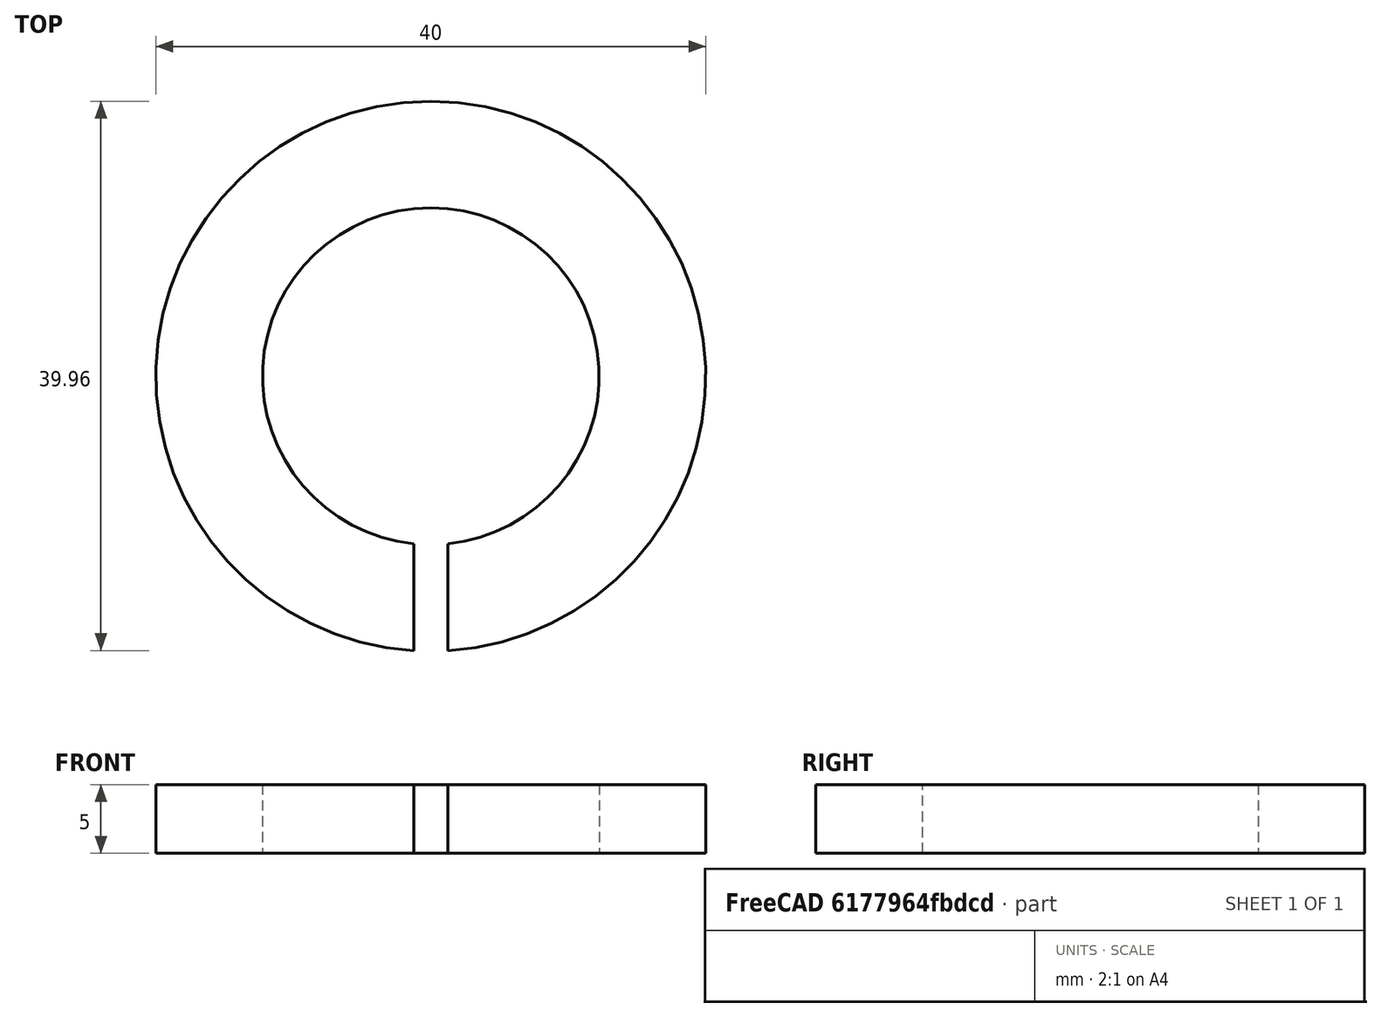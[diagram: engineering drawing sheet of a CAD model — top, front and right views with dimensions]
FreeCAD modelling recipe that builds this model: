
FCSTD DOCUMENT  (FreeCAD 0.15R4651 (Git))
Label: Federring_DIN127-B24
License: All rights reserved
LicenseURL: http://de.wikipedia.org/wiki/Alle_Rechte_vorbehalten
objects: Sketcher::SketchObject×1, PartDesign::Pad×1
note: 3 computed .brp shape members not serialized (recipe doc carries the construction recipe); baked Part::Feature solids carry a one-line shape summary decoded from their .brp

FEATURE [Sketcher::SketchObject] Sketch
  sketch-geometry (4):
    g0: ArcOfCircle CenterX=0 CenterY=0 CenterZ=0 NormalX=0 NormalY=0 NormalZ=1 Radius=12.25 StartAngle=4.81461 EndAngle=10.8934
    g1: ArcOfCircle CenterX=0 CenterY=0 CenterZ=0 NormalX=0 NormalY=0 NormalZ=1 Radius=20 StartAngle=4.77493 EndAngle=10.933
    g2: LineSegment StartX=1.25 StartY=-12.1861 StartZ=0 EndX=1.25 EndY=-19.9609 EndZ=0
    g3: LineSegment StartX=-1.25 StartY=-19.9609 StartZ=0 EndX=-1.25 EndY=-12.1861 EndZ=0
  constraints (12):
    c: Coincident(g0,g-1)
    c: Coincident(g1,g-1)
    c: Vertical(g2)
    c: Vertical(g3)
    c: Coincident(g0,g2)
    c: Coincident(g0,g3)
    c: Coincident(g1,g2)
    c: Coincident(g1,g3)
    c: Symmetric(g1,g1,g-2)
    c: Radius(g0) = 12.25
    c: Radius(g1) = 20
    c: DistanceX(g1,g1) = -2.5
FEATURE [PartDesign::Pad] Pad  label="Federring DIN 127-B 24 #"
  Length = 5
  Length2 = 100
  Midplane = true
  Sketch = -> Sketch
  Type = 0
